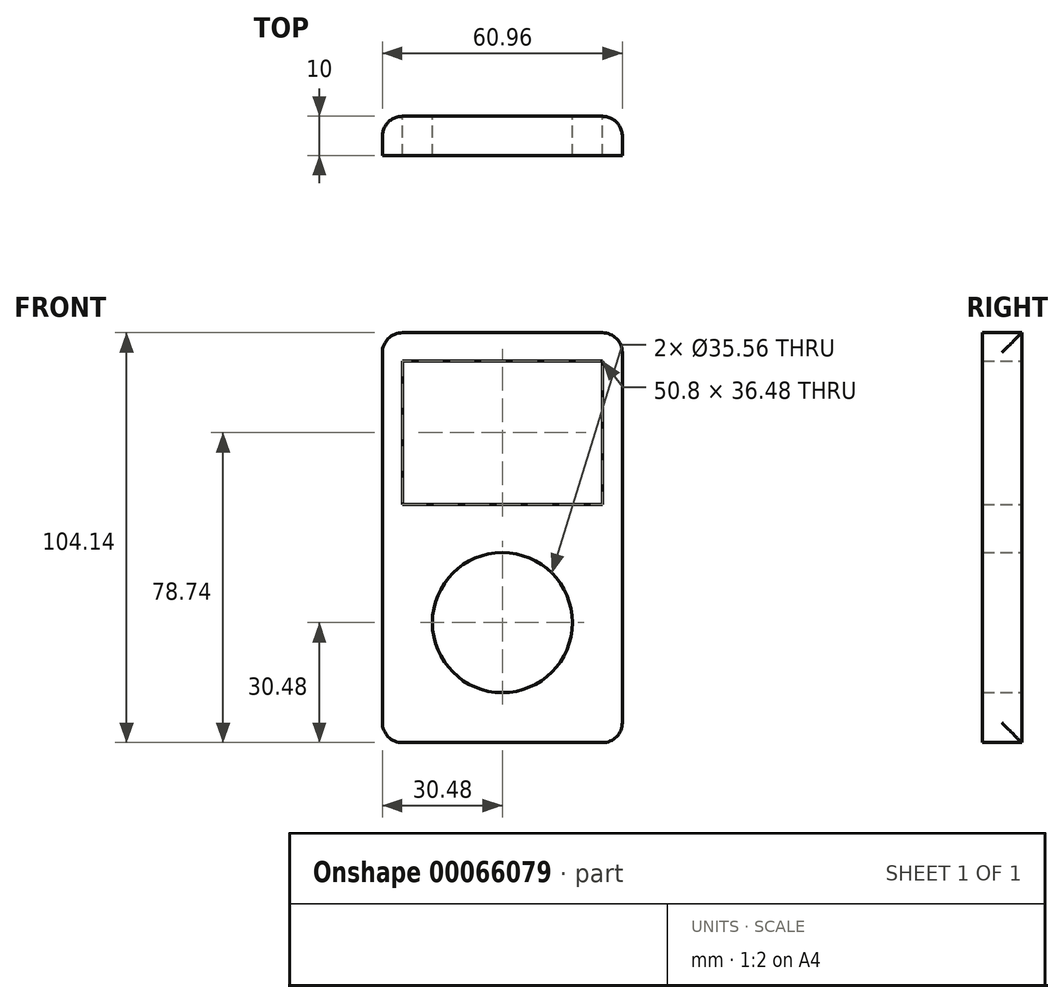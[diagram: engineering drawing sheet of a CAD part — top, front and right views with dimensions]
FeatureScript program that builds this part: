
annotation { "Feature Type Name" : "Feature", "Feature Type Description" : "" }
export const myFeature = defineFeature(function(context is Context, id is Id, definition is map)
    precondition{}
    {
        {
            var Q0;
            Q0=qCreatedBy(makeId("Front.planeOp"),FACE);
            var sketch = newSketch(context, id + "F0", { "sketchPlane" : qUnion([Q0])});
            skLineSegment(sketch, "E0.rect.bottom", {"start": v(-30.48, -52.07) * mm, "end": v(30.48, -52.07) * mm});
            skLineSegment(sketch, "E0.rect.top", {"start": v(-30.48, 52.07) * mm, "end": v(30.48, 52.07) * mm});
            skLineSegment(sketch, "E0.rect.left", {"start": v(-30.48, -52.07) * mm, "end": v(-30.48, 52.07) * mm});
            skLineSegment(sketch, "E0.rect.right", {"start": v(30.48, -52.07) * mm, "end": v(30.48, 52.07) * mm});
            skPoint(sketch, "E0.rect.middle", {"position": v(0, 0) * mm});
            skLineSegment(sketch, "E1.rect.bottom", {"start": v(25.4, 8.43) * mm, "end": v(-25.4, 8.43) * mm});
            skLineSegment(sketch, "E1.rect.top", {"start": v(25.4, 44.91) * mm, "end": v(-25.4, 44.91) * mm});
            skLineSegment(sketch, "E1.rect.left", {"start": v(25.4, 8.43) * mm, "end": v(25.4, 44.91) * mm});
            skLineSegment(sketch, "E1.rect.right", {"start": v(-25.4, 8.43) * mm, "end": v(-25.4, 44.91) * mm});
            skPoint(sketch, "E1.rect.middle", {"position": v(0, 26.67) * mm});
            skCircle(sketch, "E2", {"center": v(0, -21.59) * mm, "radius": 17.78 * mm});
            skCircle(sketch, "E3", {"center": v(0, -21.59) * mm, "radius": 7.62 * mm});
            skSolve(sketch);
        }
        {
            var Q0;
            Q0 = qSketchRegion(id + "F0", true);
            extrude(context, id + "F1", {"entities" : qUnion([Q0]), "depth" : 10 * mm});
        }
        {
            var Q0;
            Q0=makeQuery(id+"F1.opExtrude","SWEPT_EDGE",EDGE,{"disambiguationData":[OSD([sQuery(id+"F0.wireOp",EDGE,"E0.rect.top"),sQuery(id+"F0.wireOp",EDGE,"E0.rect.left")])]});
            var Q1;
            Q1=makeQuery(id+"F1.opExtrude","SWEPT_EDGE",EDGE,{"disambiguationData":[OSD([sQuery(id+"F0.wireOp",EDGE,"E0.rect.bottom"),sQuery(id+"F0.wireOp",EDGE,"E0.rect.left")])]});
            var Q2;
            Q2=makeQuery(id+"F1.opExtrude","SWEPT_EDGE",EDGE,{"disambiguationData":[OSD([sQuery(id+"F0.wireOp",EDGE,"E0.rect.top"),sQuery(id+"F0.wireOp",EDGE,"E0.rect.right")])]});
            var Q3;
            Q3=makeQuery(id+"F1.opExtrude","CAP_EDGE",EDGE,{"disambiguationData":[OSD([sQuery(id+"F0.wireOp",EDGE,"E0.rect.left")])],"isStart":true});
            var Q4;
            Q4=makeQuery(id+"F1.opExtrude","CAP_EDGE",EDGE,{"disambiguationData":[OSD([sQuery(id+"F0.wireOp",EDGE,"E0.rect.right")])],"isStart":true});
            var Q5;
            Q5=makeQuery(id+"F1.opExtrude","SWEPT_EDGE",EDGE,{"disambiguationData":[OSD([sQuery(id+"F0.wireOp",EDGE,"E0.rect.bottom"),sQuery(id+"F0.wireOp",EDGE,"E0.rect.right")])]});
            fillet(context, id + "F2", {"entities" : qUnion([Q0, Q1, Q2, Q3, Q4, Q5]), "radius" : 5.08 * mm, "tangentPropagation" : true, "allowEdgeOverflow" : false});
        }
    });
